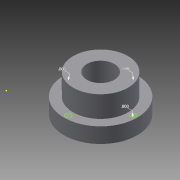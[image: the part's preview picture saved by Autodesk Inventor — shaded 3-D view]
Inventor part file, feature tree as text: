
AUTODESK INVENTOR PART (.ipt)
format: ipt  version: 2015 (Build 190159000, 159)  size: 93,696 bytes
history: native  units: in
note: dims shown in document units (in); Inventor stores cm internally (conversion verified against a paired STEP export)
features: sketch x3, extrude x3
ambient origin geometry x8: Origin, YZ Plane, XZ Plane, XY Plane, X Axis, Y Axis, Z Axis, Center Point
bodies: Solid1 (feature_tree)
feature tree (6):
  sketch  "Sketch1"  dims[d0=12.0in d1=9.0in]
  extrude  "Extrusion1"  Depth=9.0in
  extrude  "Extrusion2"  Depth=6.0in TaperAngle=0.0deg
  extrude  "Extrusion3"  Depth=4.5in
  sketch  "Sketch3"  dims[d6=4.5in d7=4.5in d8=6.0in d9=0.0in d10=0.8in d11=0.8in d12=0.8in]
  sketch  "Sketch2"  dims[d2=2.5in d3=0.0in d4=6.0in d5=0.0in]
